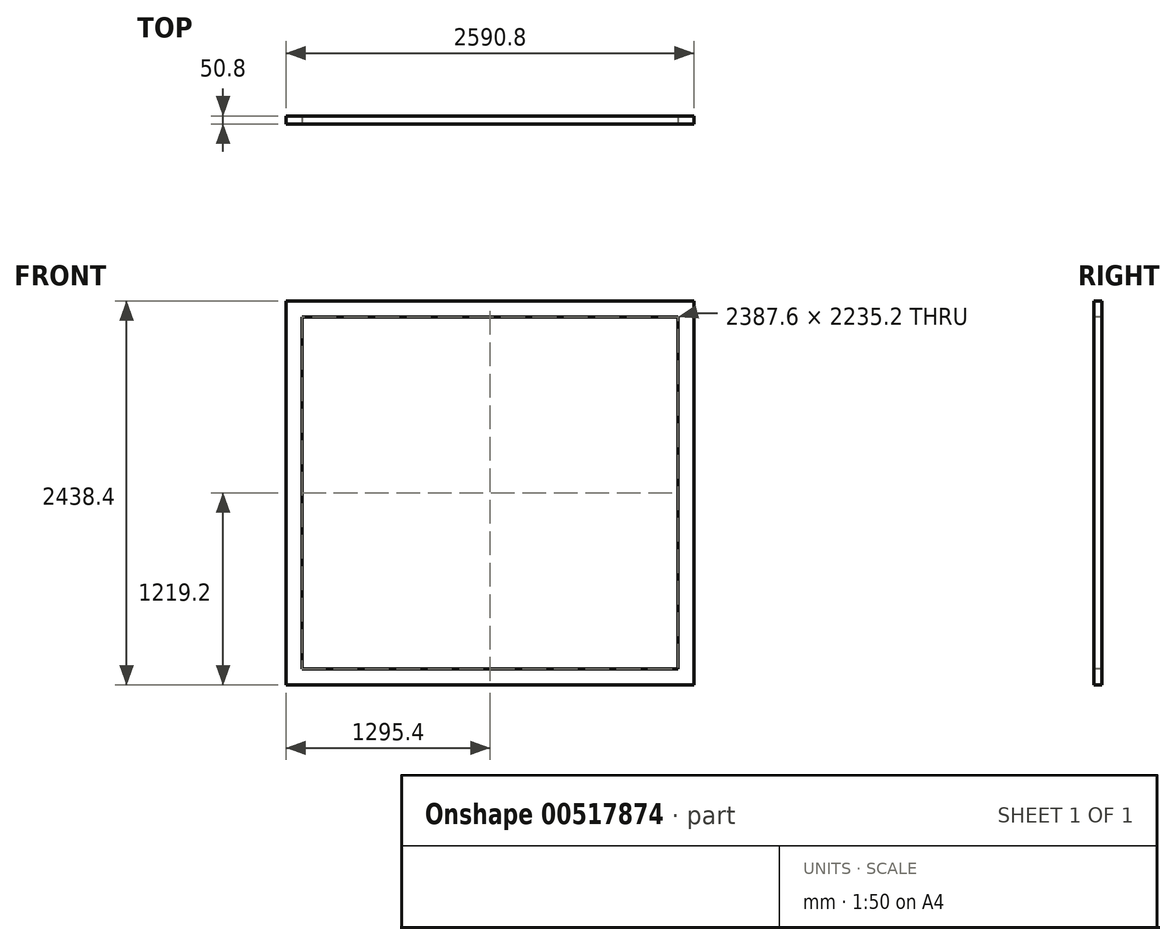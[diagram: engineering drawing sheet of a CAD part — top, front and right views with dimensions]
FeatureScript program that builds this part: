
annotation { "Feature Type Name" : "Feature", "Feature Type Description" : "" }
export const myFeature = defineFeature(function(context is Context, id is Id, definition is map)
    precondition{}
    {
        {
            var Q0;
            Q0=qCreatedBy(makeId("Front.planeOp"),FACE);
            var sketch = newSketch(context, id + "F0", { "sketchPlane" : qUnion([Q0])});
            skLineSegment(sketch, "E0.bottom", {"start": v(0, 0) * mm, "end": v(2387.6, 0) * mm});
            skLineSegment(sketch, "E0.top", {"start": v(0, 2235.2) * mm, "end": v(2387.6, 2235.2) * mm});
            skLineSegment(sketch, "E0.left", {"start": v(0, 0) * mm, "end": v(0, 2235.2) * mm});
            skLineSegment(sketch, "E0.right", {"start": v(2387.6, 0) * mm, "end": v(2387.6, 2235.2) * mm});
            skLineSegment(sketch, "E1.0", {"start": v(2489.2, -101.6) * mm, "end": v(2489.2, 2336.8) * mm});
            skLineSegment(sketch, "E1.1", {"start": v(-101.6, -101.6) * mm, "end": v(2489.2, -101.6) * mm});
            skLineSegment(sketch, "E1.2", {"start": v(-101.6, -101.6) * mm, "end": v(-101.6, 2336.8) * mm});
            skLineSegment(sketch, "E1.3", {"start": v(-101.6, 2336.8) * mm, "end": v(2489.2, 2336.8) * mm});
            skSolve(sketch);
        }
        {
            var Q0;
            Q0 = qSketchRegion(id + "F0", true);
            extrude(context, id + "F1", {"entities" : qUnion([Q0]), "oppositeDirection" : true, "depth" : 50.8 * mm, "offsetDistance" : 25.4 * mm});
        }
    });
